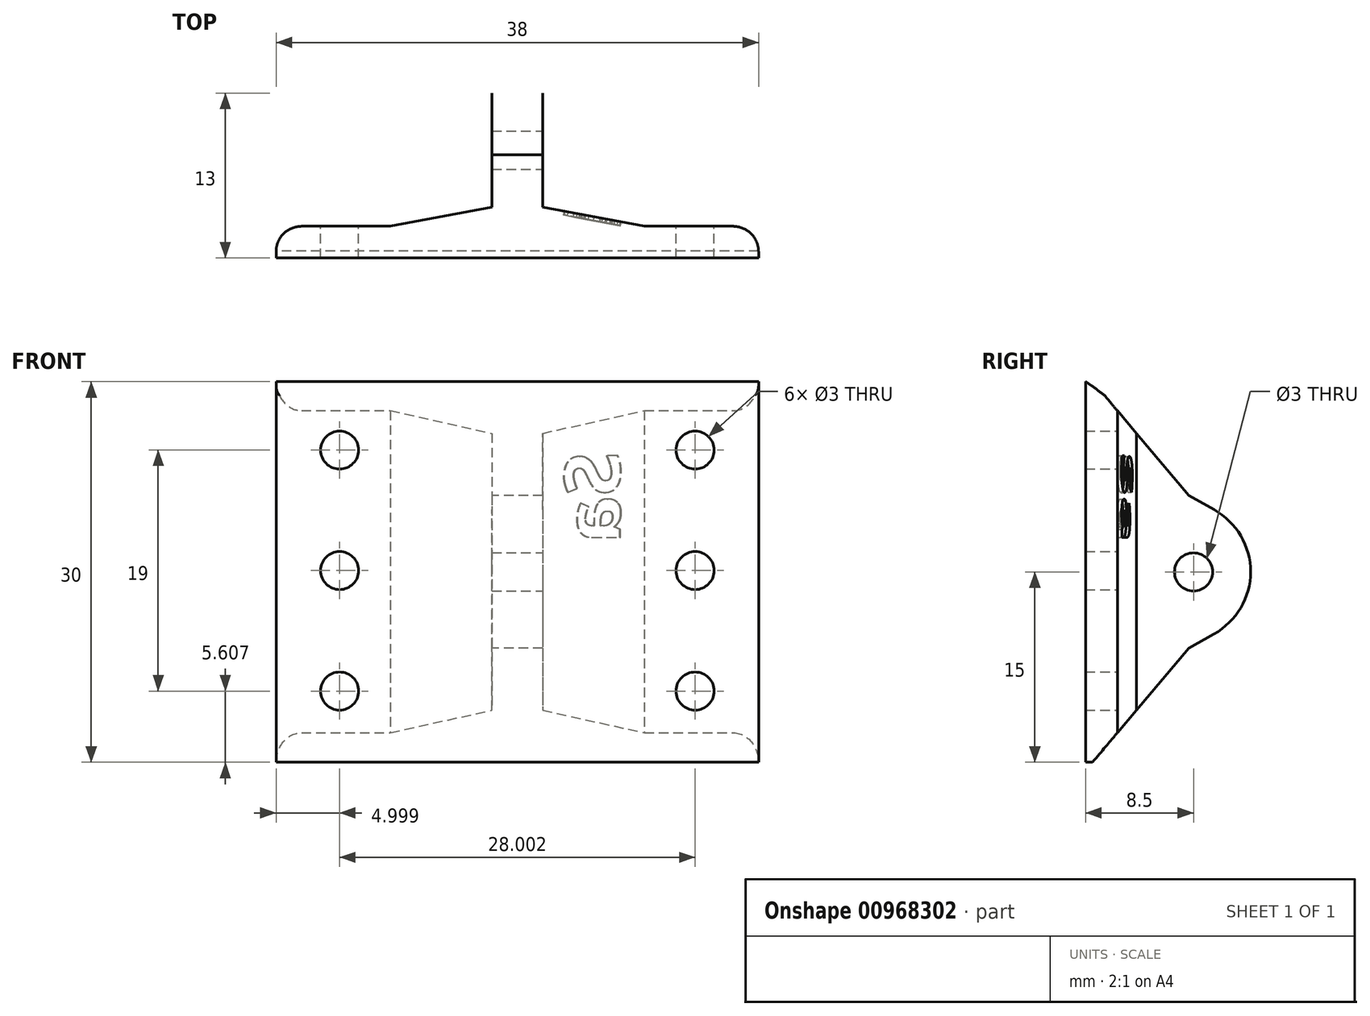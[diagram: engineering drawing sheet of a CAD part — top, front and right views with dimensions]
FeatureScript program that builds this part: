
annotation { "Feature Type Name" : "Feature", "Feature Type Description" : "" }
export const myFeature = defineFeature(function(context is Context, id is Id, definition is map)
    precondition{}
    {
        {
            var Q0;
            Q0=qCreatedBy(makeId("Top.planeOp"),FACE);
            var sketch = newSketch(context, id + "F0", { "sketchPlane" : qUnion([Q0])});
            skLineSegment(sketch, "E0", {"start": v(0, 0) * mm, "end": v(38, 0) * mm});
            skLineSegment(sketch, "E1", {"start": v(38, 0) * mm, "end": v(38, 2.5) * mm});
            skLineSegment(sketch, "E2", {"start": v(21, 4) * mm, "end": v(21, 13) * mm});
            skLineSegment(sketch, "E3", {"start": v(21, 13) * mm, "end": v(17, 13) * mm});
            skLineSegment(sketch, "E4", {"start": v(0, 2.5) * mm, "end": v(0, 0) * mm});
            skLineSegment(sketch, "E5", {"start": v(17, 13) * mm, "end": v(17, 4) * mm});
            skLineSegment(sketch, "E6", {"start": v(17, 4) * mm, "end": v(9, 2.5) * mm});
            skLineSegment(sketch, "E7", {"start": v(9, 2.5) * mm, "end": v(0, 2.5) * mm});
            skLineSegment(sketch, "E8", {"start": v(38, 2.5) * mm, "end": v(29, 2.5) * mm});
            skLineSegment(sketch, "E9", {"start": v(29, 2.5) * mm, "end": v(21, 4) * mm});
            skLineSegment(sketch, "E10", {"start": v(17, 4) * mm, "end": v(21, 4) * mm});
            skSolve(sketch);
        }
        {
            var Q0;
            Q0=qSketchRegion(id+"F0",true);
            var Q1;
            Q1=qSketchRegion(id+"F2",true);
            extrude(context, id + "F1", {"entities" : qUnion([Q0, Q1]), "depth" : 30 * mm, "offsetDistance" : 25 * mm});
        }
        {
            var Q0;
            Q0=qCreatedBy(makeId("Right.planeOp"),FACE);
            var sketch = newSketch(context, id + "F2", { "sketchPlane" : qUnion([Q0])});
            skLineSegment(sketch, "E11", {"start": v(14, 17.73) * mm, "end": v(8.13, 21.02) * mm});
            skLineSegment(sketch, "E12", {"start": v(8.13, 21.02) * mm, "end": v(0.55, 30.03) * mm});
            skLineSegment(sketch, "E13", {"start": v(14, 12.28) * mm, "end": v(8.13, 9) * mm});
            skLineSegment(sketch, "E14", {"start": v(8.13, 9) * mm, "end": v(0.55, 0) * mm});
            skLineSegment(sketch, "E15", {"start": v(0.55, 0) * mm, "end": v(14, 0) * mm});
            skLineSegment(sketch, "E16", {"start": v(14, 0) * mm, "end": v(14, 12.28) * mm});
            skLineSegment(sketch, "E17", {"start": v(14, 17.73) * mm, "end": v(14, 30) * mm});
            skLineSegment(sketch, "E18", {"start": v(14, 30) * mm, "end": v(0.55, 30.03) * mm});
            skSolve(sketch);
        }
        {
            var Q0;
            Q0=makeQuery(id+"F1.opExtrude","SWEPT_FACE",FACE,{"disambiguationData":[OSD([sQuery(id+"F0.wireOp",EDGE,"E5")])]});
            var sketch = newSketch(context, id + "F3", { "sketchPlane" : qUnion([Q0])});
            skPoint(sketch, "E19", {"position": v(-8.5, 15) * mm});
            skPoint(sketch, "E19.positionSnap0", {"position": v(-8.5, 0) * mm});
            skPoint(sketch, "E19.positionSnap1", {"position": v(-4, 15) * mm});
            skSolve(sketch);
        }
        {
            var Q0;
            Q0=qSketchRegion(id+"F2",true);
            extrude(context, id + "F4", {"entities" : qUnion([Q0]), "operationType" : NewBodyOperationType.REMOVE, "depth" : 39 * mm, "offsetDistance" : 25 * mm});
        }
        {
            var Q0;
            Q0=sQuery(id+"F3.wireOp",VERTEX,"E19");
            var Q1;
            Q1=makeQuery(id+"F1.opExtrude","SWEPT_BODY",BODY,{"disambiguationData":[OSD([sQuery(id+"F0.wireOp",EDGE,"E0"),sQuery(id+"F0.wireOp",EDGE,"E1"),sQuery(id+"F0.wireOp",EDGE,"E2"),sQuery(id+"F0.wireOp",EDGE,"E3"),sQuery(id+"F0.wireOp",EDGE,"E4"),sQuery(id+"F0.wireOp",EDGE,"E5"),sQuery(id+"F0.wireOp",EDGE,"E6"),sQuery(id+"F0.wireOp",EDGE,"E7"),sQuery(id+"F0.wireOp",EDGE,"E8"),sQuery(id+"F0.wireOp",EDGE,"E9")])]});
            hole(context, id + "F5", {"style" : HoleStyle.SIMPLE, "endStyle" : HoleEndStyle.THROUGH, "holeDiameter" : 3 * mm, "majorDiameter" : 5 * mm, "isTappedThrough" : true, "tappedDepth" : 12 * mm, "tapClearance" : 3, "locations" : qUnion([Q0]), "scope" : qUnion([Q1]), "startStyle" : HoleStartStyle.PART});
        }
        {
            var Q0;
            Q0=makeQuery(id+"F4.boolean.opBoolean","COPY",EDGE,{"derivedFrom":makeQuery(id+"F4.opExtrude","SWEPT_EDGE",EDGE,{"disambiguationData":[OSD([sQuery(id+"F2.wireOp",EDGE,"E14"),sQuery(id+"F2.wireOp",EDGE,"E15")])]})});
            var Q1;
            Q1=makeQuery(id+"F4.boolean.opBoolean","INTERSECT",EDGE,{"derivedFrom":[makeQuery(id+"F1.opExtrude","CAP_FACE",FACE,{"disambiguationData":[OSD([sQuery(id+"F0.wireOp",EDGE,"E0"),sQuery(id+"F0.wireOp",EDGE,"E1"),sQuery(id+"F0.wireOp",EDGE,"E2"),sQuery(id+"F0.wireOp",EDGE,"E3"),sQuery(id+"F0.wireOp",EDGE,"E4"),sQuery(id+"F0.wireOp",EDGE,"E5"),sQuery(id+"F0.wireOp",EDGE,"E6"),sQuery(id+"F0.wireOp",EDGE,"E7"),sQuery(id+"F0.wireOp",EDGE,"E8"),sQuery(id+"F0.wireOp",EDGE,"E9")])],"isStart":false}),makeQuery(id+"F4.opExtrude","SWEPT_FACE",FACE,{"disambiguationData":[OSD([sQuery(id+"F2.wireOp",EDGE,"E12")])]})]});
            fillet(context, id + "F6", {"entities" : qUnion([Q0, Q1]), "radius" : 4 * mm, "tangentPropagation" : true, "rho" : 0.1, "crossSection" : FilletCrossSection.CONIC, "allowEdgeOverflow" : false});
        }
        {
            var Q0;
            Q0=makeQuery(id+"F1.opExtrude","SWEPT_EDGE",EDGE,{"disambiguationData":[OSD([sQuery(id+"F0.wireOp",EDGE,"E4"),sQuery(id+"F0.wireOp",EDGE,"E7")])]});
            var Q1;
            Q1=makeQuery(id+"F1.opExtrude","SWEPT_EDGE",EDGE,{"disambiguationData":[OSD([sQuery(id+"F0.wireOp",EDGE,"E1"),sQuery(id+"F0.wireOp",EDGE,"E8")])]});
            fillet(context, id + "F7", {"entities" : qUnion([Q0, Q1]), "radius" : 2 * mm, "tangentPropagation" : true, "allowEdgeOverflow" : false});
        }
        {
            var Q0;
            Q0=qCreatedBy(makeId("Front.planeOp"),FACE);
            var sketch = newSketch(context, id + "F8", { "sketchPlane" : qUnion([Q0])});
            skPoint(sketch, "E20", {"position": v(33, 24.6) * mm});
            skPoint(sketch, "E21", {"position": v(33, 15.1) * mm});
            skPoint(sketch, "E22", {"position": v(33, 5.6) * mm});
            skPoint(sketch, "E23", {"position": v(5, 5.6) * mm});
            skPoint(sketch, "E24", {"position": v(5, 15.1) * mm});
            skPoint(sketch, "E25", {"position": v(5, 24.6) * mm});
            skSolve(sketch);
        }
        {
            var Q0;
            Q0=sQuery(id+"F8.wireOp",VERTEX,"E20");
            var Q1;
            Q1=sQuery(id+"F8.wireOp",VERTEX,"E21");
            var Q2;
            Q2=sQuery(id+"F8.wireOp",VERTEX,"E22");
            var Q3;
            Q3=sQuery(id+"F8.wireOp",VERTEX,"E25");
            var Q4;
            Q4=sQuery(id+"F8.wireOp",VERTEX,"E24");
            var Q5;
            Q5=sQuery(id+"F8.wireOp",VERTEX,"E23");
            var Q6;
            Q6=makeQuery(id+"F1.opExtrude","SWEPT_BODY",BODY,{"disambiguationData":[OSD([sQuery(id+"F0.wireOp",EDGE,"E0"),sQuery(id+"F0.wireOp",EDGE,"E1"),sQuery(id+"F0.wireOp",EDGE,"E2"),sQuery(id+"F0.wireOp",EDGE,"E3"),sQuery(id+"F0.wireOp",EDGE,"E4"),sQuery(id+"F0.wireOp",EDGE,"E5"),sQuery(id+"F0.wireOp",EDGE,"E6"),sQuery(id+"F0.wireOp",EDGE,"E7"),sQuery(id+"F0.wireOp",EDGE,"E8"),sQuery(id+"F0.wireOp",EDGE,"E9")])]});
            hole(context, id + "F9", {"style" : HoleStyle.SIMPLE, "endStyle" : HoleEndStyle.THROUGH, "holeDiameter" : 3 * mm, "majorDiameter" : 5 * mm, "isTappedThrough" : true, "tappedDepth" : 12 * mm, "tapClearance" : 3, "locations" : qUnion([Q0, Q1, Q2, Q3, Q4, Q5]), "scope" : qUnion([Q6]), "startStyle" : HoleStartStyle.PART});
        }
        {
            var Q0;
            Q0=makeQuery(id+"F1.opExtrude","SWEPT_FACE",FACE,{"disambiguationData":[OSD([sQuery(id+"F0.wireOp",EDGE,"E9")])]});
            var sketch = newSketch(context, id + "F10", { "sketchPlane" : qUnion([Q0])});
            skText(sketch, "E26", { "text": "Sa", "fontName": "OpenSans-Bold.ttf"});
            const initialGuessF10  = {"E26": [-0.02614, 0.02444, 0, -1, 0.00448]};
            skSetInitialGuess(sketch, initialGuessF10);
            skSolve(sketch);
        }
        {
            var Q0;
            Q0=qSketchRegion(id+"F10",true);
            extrude(context, id + "F11", {"entities" : qUnion([Q0]), "operationType" : NewBodyOperationType.REMOVE, "oppositeDirection" : true, "depth" : 0.3 * mm, "offsetDistance" : 25 * mm});
        }
        {
            var Q0;
            Q0=makeQuery(id+"F4.boolean.opBoolean","INTERSECT",EDGE,{"derivedFrom":[makeQuery(id+"F1.opExtrude","SWEPT_FACE",FACE,{"disambiguationData":[OSD([sQuery(id+"F0.wireOp",EDGE,"E3")])]}),makeQuery(id+"F4.opExtrude","SWEPT_FACE",FACE,{"disambiguationData":[OSD([sQuery(id+"F2.wireOp",EDGE,"E11")])]})]});
            var Q1;
            Q1=makeQuery(id+"F4.boolean.opBoolean","INTERSECT",EDGE,{"derivedFrom":[makeQuery(id+"F1.opExtrude","SWEPT_FACE",FACE,{"disambiguationData":[OSD([sQuery(id+"F0.wireOp",EDGE,"E3")])]}),makeQuery(id+"F4.opExtrude","SWEPT_FACE",FACE,{"disambiguationData":[OSD([sQuery(id+"F2.wireOp",EDGE,"E13")])]})]});
            fillet(context, id + "F12", {"entities" : qUnion([Q0, Q1]), "radius" : 5.63 * mm, "tangentPropagation" : true, "allowEdgeOverflow" : false});
        }
    });
